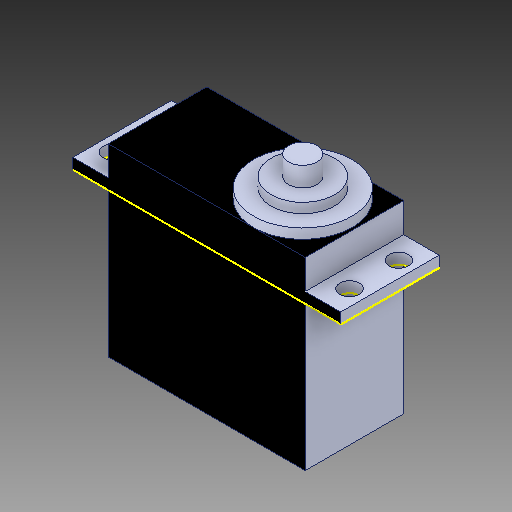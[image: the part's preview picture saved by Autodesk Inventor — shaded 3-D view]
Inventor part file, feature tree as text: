
AUTODESK INVENTOR PART (.ipt)
format: ipt  version: 2018 (Build 220112000, 112)  size: 165,376 bytes
history: native  units: mm
features: other x3, sketch x1
ambient origin geometry x8: Origin, YZ Plane, XZ Plane, XY Plane, X Axis, Y Axis, Z Axis, Center Point
bodies: Solid1 (feature_tree)
feature tree (4):
  other  "SERVOMG996R.ipt"
  other  "Solid1::SERVOMG996R.ipt"
  other  "TaggingFeature1"
  sketch  "Sketch7"  dims[d0=10.0mm]
